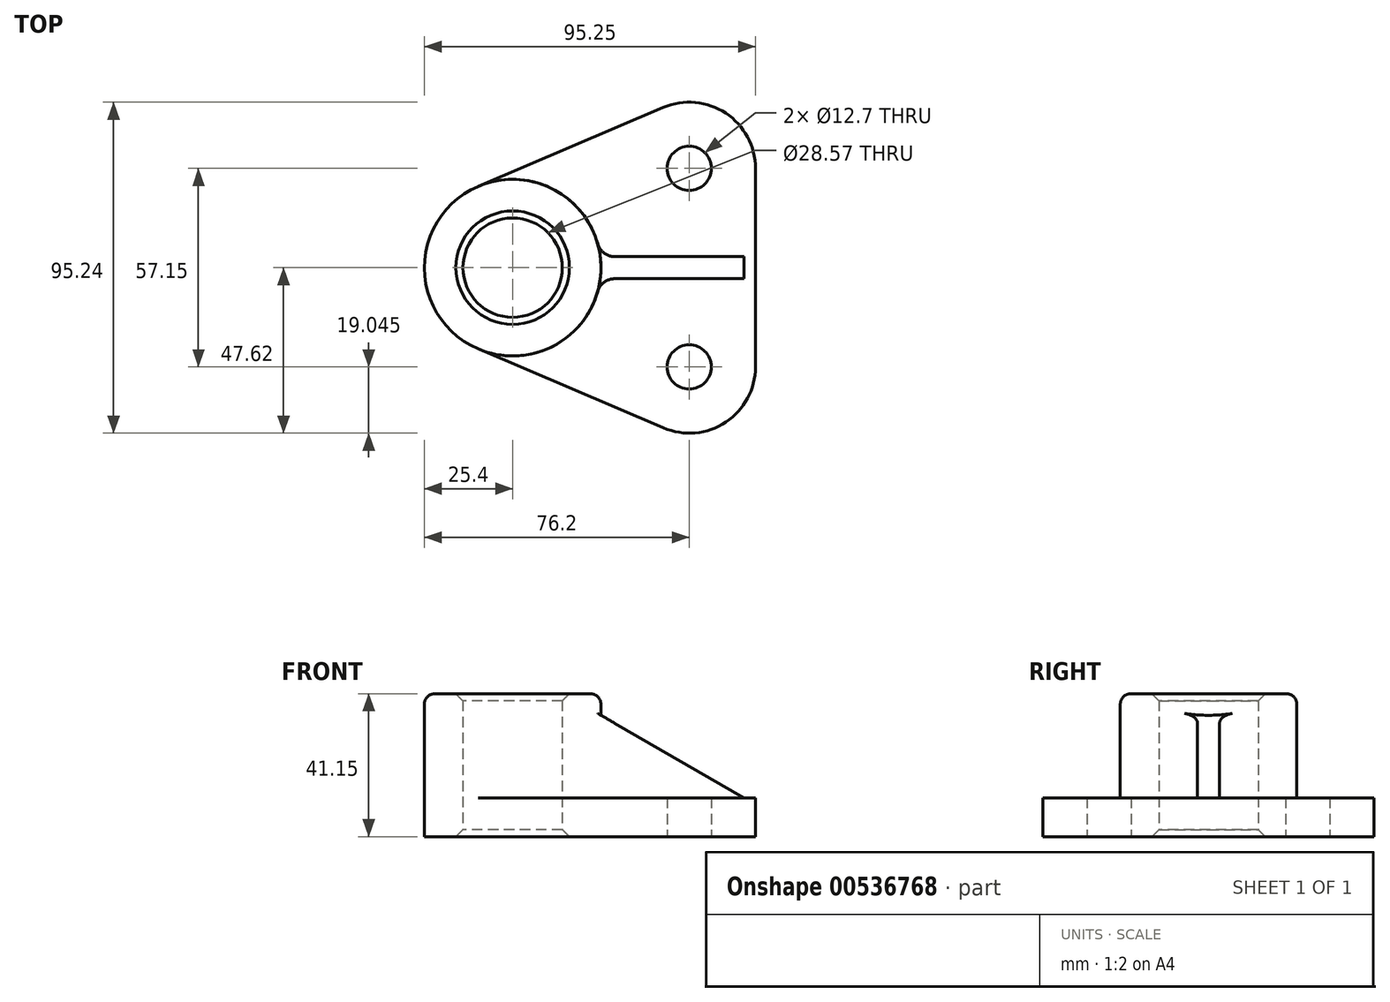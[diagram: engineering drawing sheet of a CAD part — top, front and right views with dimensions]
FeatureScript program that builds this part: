
annotation { "Feature Type Name" : "Feature", "Feature Type Description" : "" }
export const myFeature = defineFeature(function(context is Context, id is Id, definition is map)
    precondition{}
    {
        {
            var Q0;
            Q0=qCreatedBy(makeId("Top.planeOp"),FACE);
            var sketch = newSketch(context, id + "F0", { "sketchPlane" : qUnion([Q0])});
            skCircle(sketch, "E0", {"center": v(0, 0) * mm, "radius": 25.4 * mm});
            skCircle(sketch, "E1", {"center": v(50.8, 28.58) * mm, "radius": 6.35 * mm});
            skCircle(sketch, "E2", {"center": v(50.8, -28.58) * mm, "radius": 6.35 * mm});
            skCircle(sketch, "E3", {"center": v(0, 0) * mm, "radius": 14.29 * mm});
            skLineSegment(sketch, "E4", {"start": v(-9.97, 23.36) * mm, "end": v(43.33, 46.1) * mm});
            skLineSegment(sketch, "E5", {"start": v(-9.97, -23.36) * mm, "end": v(43.33, -46.1) * mm});
            skLineSegment(sketch, "E6", {"start": v(69.85, -28.58) * mm, "end": v(69.85, 28.58) * mm});
            skLineSegment(sketch, "E7", {"start": v(25.4, 0) * mm, "end": v(69.85, 0) * mm, "construction": true});
            skArc(sketch, "E8", {"start": v(43.33, 46.1) * mm, "mid": v(40.3, 12.68) * mm, "end": v(69.85, 28.58) * mm, "construction": true});
            skArc(sketch, "E9", {"start": v(69.85, 28.58) * mm, "mid": v(61.3, 44.47) * mm, "end": v(43.33, 46.1) * mm});
            skArc(sketch, "E10", {"start": v(43.33, -46.1) * mm, "mid": v(61.3, -44.47) * mm, "end": v(69.85, -28.57) * mm});
            skArc(sketch, "E11", {"start": v(69.85, -28.58) * mm, "mid": v(40.3, -12.68) * mm, "end": v(43.33, -46.1) * mm, "construction": true});
            skSolve(sketch);
        }
        {
            var Q0;
            Q0=makeQuery(id+"F0.imprint","IMPRINT",FACE,{"disambiguationData":[TD([[makeQuery(id+"F0.imprint","IMPRINT",EDGE,{"derivedFrom":sQuery(id+"F0.wireOp",EDGE,"E1")}),-1.0]])]});
            extrude(context, id + "F1", {"entities" : qUnion([Q0]), "depth" : 11.18 * mm, "offsetDistance" : 25.4 * mm});
        }
        {
            var Q0;
            Q0=makeQuery(id+"F0.imprint","IMPRINT",FACE,{"disambiguationData":[TD([[makeQuery(id+"F0.imprint","IMPRINT",EDGE,{"derivedFrom":sQuery(id+"F0.wireOp",EDGE,"E3")}),-1.0]])]});
            extrude(context, id + "F2", {"entities" : qUnion([Q0]), "operationType" : NewBodyOperationType.ADD, "depth" : 41.15 * mm, "offsetDistance" : 25.4 * mm});
        }
        {
            var Q0;
            Q0=makeQuery(id+"F2.opExtrude","CAP_EDGE",EDGE,{"disambiguationData":[OSD([sQuery(id+"F0.wireOp",EDGE,"E0")])],"isStart":false});
            fillet(context, id + "F3", {"entities" : qUnion([Q0]), "radius" : 3.05 * mm, "tangentPropagation" : true, "allowEdgeOverflow" : false});
        }
        {
            var Q0;
            Q0=qCreatedBy(makeId("Front.planeOp"),FACE);
            var sketch = newSketch(context, id + "F4", { "sketchPlane" : qUnion([Q0])});
            skLineSegment(sketch, "E12", {"start": v(66.55, 11.18) * mm, "end": v(22.1, 11.18) * mm});
            skLineSegment(sketch, "E13", {"start": v(22.1, 11.18) * mm, "end": v(22.1, 36.84) * mm});
            skLineSegment(sketch, "E14", {"start": v(22.1, 36.84) * mm, "end": v(66.55, 11.18) * mm});
            skLineSegment(sketch, "E15", {"start": v(66.55, 11.18) * mm, "end": v(69.85, 11.18) * mm, "construction": true});
            skSolve(sketch);
        }
        {
            var Q0;
            Q0=makeQuery(id+"F4.imprint","IMPRINT",FACE,{"disambiguationData":[TD([[makeQuery(id+"F4.imprint","IMPRINT",EDGE,{"derivedFrom":sQuery(id+"F4.wireOp",EDGE,"E12")}),-1.0]])]});
            extrude(context, id + "F5", {"entities" : qUnion([Q0]), "operationType" : NewBodyOperationType.ADD, "endBound" : BoundingType.SYMMETRIC, "depth" : 6.35 * mm, "offsetDistance" : 25.4 * mm});
        }
        {
            var Q0;
            {var subQ0=sQuery(id+"F0.wireOp",EDGE,"E5");var subQ1=sQuery(id+"F0.wireOp",EDGE,"E0");Q0=makeQuery(id+"F5.boolean.opBoolean","SPLIT",EDGE,{"disambiguationData":[TD([makeQuery(id+"F1.opExtrude","SWEPT_FACE",FACE,{"disambiguationData":[OSD([subQ0])]})])],"derivedFrom":makeQuery(id+"F1.opExtrude","CAP_EDGE",EDGE,{"disambiguationData":[OSD([subQ1])],"isStart":false})});}
            var Q1;
            Q1=makeQuery(id+"F5.boolean.opBoolean","INTERSECT",EDGE,{"derivedFrom":[makeQuery(id+"F2.opExtrude","SWEPT_FACE",FACE,{"disambiguationData":[OSD([sQuery(id+"F0.wireOp",EDGE,"E0")])]}),makeQuery(id+"F5.opExtrude","CAP_FACE",FACE,{"disambiguationData":[OSD([sQuery(id+"F4.wireOp",EDGE,"E12"),sQuery(id+"F4.wireOp",EDGE,"E13"),sQuery(id+"F4.wireOp",EDGE,"E14")])],"isStart":false})]});
            var Q2;
            Q2=makeQuery(id+"F5.opExtrude","CAP_EDGE",EDGE,{"disambiguationData":[OSD([sQuery(id+"F4.wireOp",EDGE,"E12")])],"isStart":false});
            var Q3;
            Q3=makeQuery(id+"F5.opExtrude","CAP_EDGE",EDGE,{"disambiguationData":[OSD([sQuery(id+"F4.wireOp",EDGE,"E12")])],"isStart":true});
            var Q4;
            {var subQ0=sQuery(id+"F0.wireOp",EDGE,"E4");var subQ1=sQuery(id+"F0.wireOp",EDGE,"E0");Q4=makeQuery(id+"F5.boolean.opBoolean","SPLIT",EDGE,{"disambiguationData":[TD([makeQuery(id+"F1.opExtrude","SWEPT_FACE",FACE,{"disambiguationData":[OSD([subQ0])]})])],"derivedFrom":makeQuery(id+"F1.opExtrude","CAP_EDGE",EDGE,{"disambiguationData":[OSD([subQ1])],"isStart":false})});}
            var Q5;
            Q5=makeQuery(id+"F5.boolean.opBoolean","INTERSECT",EDGE,{"derivedFrom":[makeQuery(id+"F2.opExtrude","SWEPT_FACE",FACE,{"disambiguationData":[OSD([sQuery(id+"F0.wireOp",EDGE,"E0")])]}),makeQuery(id+"F5.opExtrude","CAP_FACE",FACE,{"disambiguationData":[OSD([sQuery(id+"F4.wireOp",EDGE,"E12"),sQuery(id+"F4.wireOp",EDGE,"E13"),sQuery(id+"F4.wireOp",EDGE,"E14")])],"isStart":true})]});
            fillet(context, id + "F6", {"entities" : qUnion([Q0, Q1, Q2, Q3, Q4, Q5]), "radius" : 5.08 * mm, "tangentPropagation" : true, "allowEdgeOverflow" : false});
        }
        {
            var Q0;
            Q0=makeQuery(id+"F2.opExtrude","CAP_EDGE",EDGE,{"disambiguationData":[OSD([sQuery(id+"F0.wireOp",EDGE,"E3")])],"isStart":false});
            var Q1;
            Q1=makeQuery(id+"F2.opExtrude","CAP_EDGE",EDGE,{"disambiguationData":[OSD([sQuery(id+"F0.wireOp",EDGE,"E3")])],"isStart":true});
            chamfer(context, id + "F7", {"entities" : qUnion([Q0, Q1]), "width" : 2.03 * mm, "tangentPropagation" : true});
        }
    });
